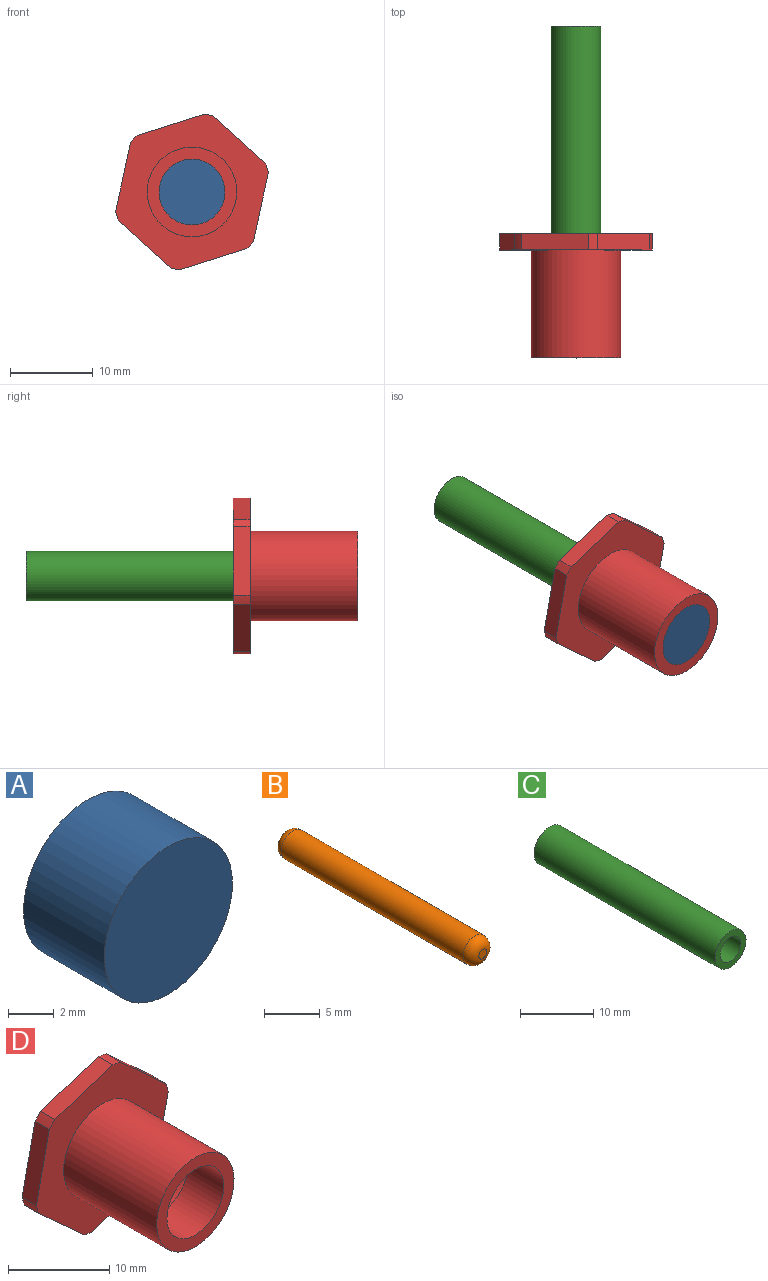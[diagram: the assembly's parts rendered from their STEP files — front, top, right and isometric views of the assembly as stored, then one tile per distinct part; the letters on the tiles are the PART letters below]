
ASSEMBLY  parts=4 mates=3
PART A: 3 faces, bbox 7.9x5x7.9 mm
  f0: cylinder r=3.97mm len=7.94mm, axis (0,1,0), area 124.7mm2, adj f1,f2
  f1: plane 7.94x7.94mm, normal (0,-1,0), area 49.5mm2, adj f0
  f2: plane 7.94x7.94mm, normal (0,1,0), area 49.5mm2, adj f0
PART B: 5 faces, bbox 3x25x3 mm
  f0: cylinder r=1.5mm len=23mm, axis (0,1,0), area 216.8mm2, adj f3,f4
  f1: plane 1x1mm, normal (0,-1,0), area 0.8mm2, adj f3
  f2: plane 1x1mm, normal (0,1,0), area 0.8mm2, adj f4
  f3: torus R=0.5mm, axis (0,-1,0), area 11.2mm2, adj f0,f1
  f4: torus R=0.5mm, axis (0,-1,0), area 11.2mm2, adj f0,f2
PART C: 4 faces, bbox 6x35x6 mm
  f0: cylinder r=2mm len=35mm, axis (0,1,0), area 439.8mm2, adj f2,f3
  f1: cylinder r=3mm len=35mm, axis (0,1,0), area 659.7mm2, adj f2,f3
  f2: plane 6x6mm, normal (0,-1,0), area 15.7mm2, adj f0,f1
  f3: plane 6x6mm, normal (0,1,0), area 15.7mm2, adj f0,f1
PART D: 19 faces, bbox 18.4x15x18.8 mm
  f0: cylinder r=2.5mm len=9.12mm, axis (0,-1,0), area 143.2mm2, adj f7,f17
  f1: cylinder r=9.5mm len=2mm, axis (0,-1,0), area 2.3mm2, adj f7,f8,f11,f16
  f2: cylinder r=9.5mm len=2mm, axis (0,-1,0), area 2.3mm2, adj f7,f8,f15,f16
  f3: cylinder r=9.5mm len=2mm, axis (0,-1,0), area 2.3mm2, adj f7,f8,f14,f15
  f4: cylinder r=9.5mm len=2mm, axis (0,-1,0), area 2.3mm2, adj f7,f8,f13,f14
  f5: cylinder r=9.5mm len=2mm, axis (0,-1,0), area 2.3mm2, adj f7,f8,f12,f13
  f6: cylinder r=9.5mm len=2mm, axis (0,-1,0), area 2.3mm2, adj f7,f8,f11,f12
  f7: plane 18.77x18.42mm, normal (0,1,0), area 229.6mm2, adj f0,f1,f2,f3,f4,f5,f6,f11
  f8: plane 18.77x18.42mm, normal (0,-1,0), area 157.6mm2, adj f1,f2,f3,f4,f5,f6,f9,f11
  f9: cylinder r=5.4mm len=13mm, axis (0,1,0), area 441.1mm2, adj f8,f10
  f10: plane 10.8x10.8mm, normal (0,-1,0), area 42.1mm2, adj f9,f18
  f11: plane 8.29x2mm, normal (0.98,0,-0.21), area 17mm2, adj f1,f6,f7,f8
  f12: plane 6.27x5.72mm, normal (0.67,0,0.74), area 17mm2, adj f5,f6,f7,f8
  f13: plane 8.09x2.57mm, normal (-0.3,0,0.95), area 17mm2, adj f4,f5,f7,f8
  f14: plane 8.29x2mm, normal (-0.98,0,0.21), area 17mm2, adj f3,f4,f7,f8
  f15: plane 6.27x5.72mm, normal (-0.67,0,-0.74), area 17mm2, adj f2,f3,f7,f8
  f16: plane 8.09x2.57mm, normal (0.3,0,-0.95), area 17mm2, adj f1,f2,f7,f8
  f17: cone r=0mm half-angle=59deg, axis (0,-1,0), area 34.8mm2, adj f0,f18
  f18: cylinder r=3.97mm len=7.94mm, axis (0,-1,0), area 124.7mm2, adj f10,f17
PLACE A t=(4,-10.54,-2.04)mm
PLACE B t=(4,1.96,-2.04)mm
PLACE C t=(4,24.46,-2.04)mm
PLACE D t=(4,-2.54,-2.04)mm
MATE cylindrical B.f0 <-> A.f0  axis (0,-1,0) through (4,-10.54,-2.04)mm
MATE cylindrical A.f0 <-> D.f0  axis (0,1,0) through (4,-10.54,-2.04)mm
MATE cylindrical C.f0 <-> A.f0  axis (0,-1,0) through (4,-10.54,-2.04)mm
